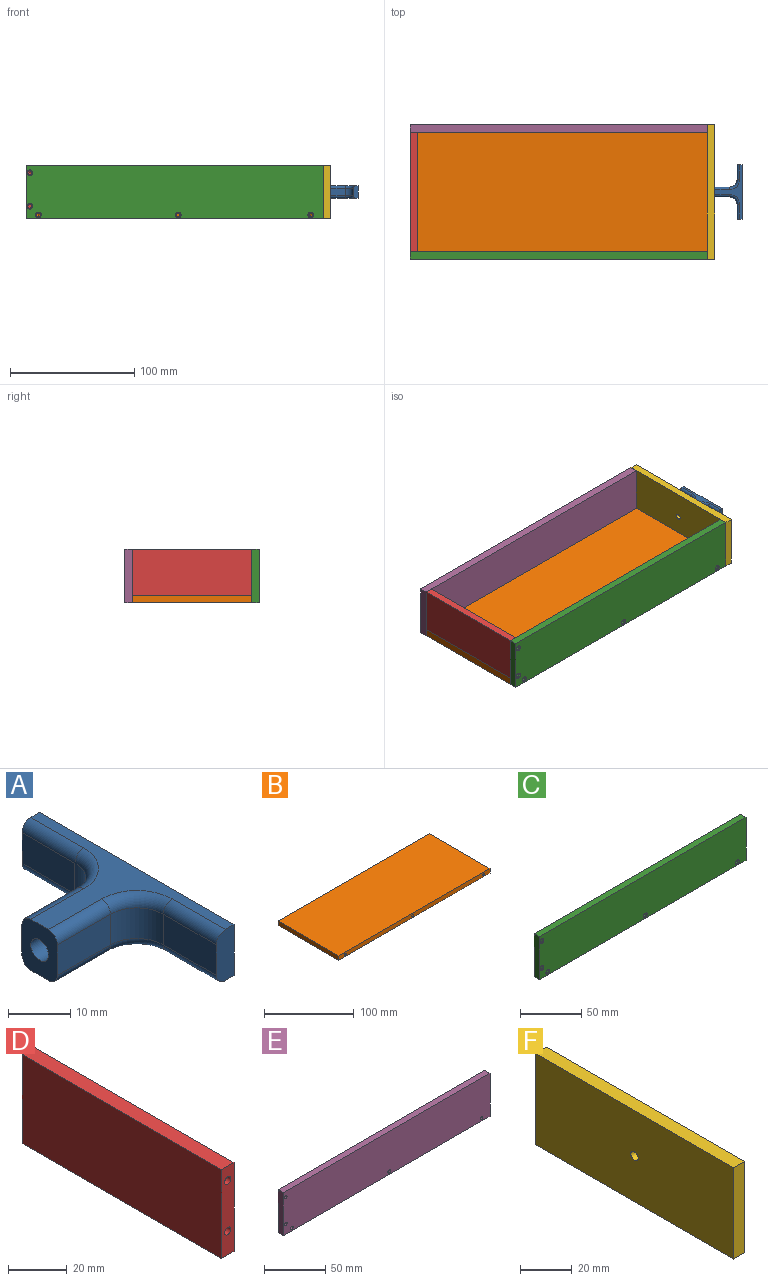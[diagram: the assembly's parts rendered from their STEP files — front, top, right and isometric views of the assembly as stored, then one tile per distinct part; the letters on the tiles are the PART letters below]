
ASSEMBLY  parts=6 mates=11
PART A: 26 faces, bbox 22.2x44x10 mm
  f0: plane 44x10mm, normal (1,0,0), area 440mm2, adj f1,f9,f10,f11
  f1: plane 10x4mm, normal (0,1,0), area 38.3mm2, adj f0,f2,f10,f11,f12,f20
  f2: plane 12x6mm, normal (-1,0,0), area 72mm2, adj f1,f3,f12,f20
  f3: cylinder r=6mm len=6mm, axis (0,0,-1), area 56.5mm2, adj f2,f4,f13,f19
  f4: plane 12x6mm, normal (0,1,0), area 72mm2, adj f3,f5,f14,f18
  f5: plane 10x8mm, normal (-1,0,0), area 64mm2, adj f4,f6,f10,f11,f14,f15,f18,f21
  f6: plane 12x6mm, normal (0,-1,0), area 72mm2, adj f5,f7,f15,f21
  f7: cylinder r=6mm len=6mm, axis (0,0,-1), area 56.5mm2, adj f6,f8,f16,f22
  f8: plane 12x6mm, normal (-1,0,0), area 72mm2, adj f7,f9,f17,f23
  f9: plane 10x4mm, normal (0,-1,0), area 38.3mm2, adj f0,f8,f10,f11,f17,f23
  f10: plane 44x22mm, normal (0,0,1), area 195.5mm2, adj f0,f1,f5,f9,f12,f13,f14,f21
  f11: plane 44x22mm, normal (0,0,-1), area 195.5mm2, adj f0,f1,f5,f9,f15,f16,f17,f18
  f12: cylinder r=2mm len=12mm, axis (0,1,0), area 37.7mm2, adj f1,f2,f10,f13
  f13: torus R=8mm, axis (0,0,1), area 33.2mm2, adj f3,f10,f12,f14
  f14: cylinder r=2mm len=12mm, axis (1,0,0), area 37.7mm2, adj f4,f5,f10,f13
  f15: cylinder r=2mm len=12mm, axis (1,0,0), area 37.7mm2, adj f5,f6,f11,f16
  f16: torus R=8mm, axis (0,0,1), area 33.2mm2, adj f7,f11,f15,f17
  f17: cylinder r=2mm len=12mm, axis (0,-1,0), area 37.7mm2, adj f8,f9,f11,f16
  f18: cylinder r=2mm len=12mm, axis (-1,0,0), area 37.7mm2, adj f4,f5,f11,f19
  f19: torus R=8mm, axis (0,0,1), area 33.2mm2, adj f3,f11,f18,f20
  f20: cylinder r=2mm len=12mm, axis (0,-1,0), area 37.7mm2, adj f1,f2,f11,f19
  f21: cylinder r=2mm len=12mm, axis (-1,0,0), area 37.7mm2, adj f5,f6,f10,f22
  f22: torus R=8mm, axis (0,0,1), area 33.2mm2, adj f7,f10,f21,f23
  f23: cylinder r=2mm len=12mm, axis (0,1,0), area 37.7mm2, adj f8,f9,f10,f22
  f24: cylinder r=2mm len=15mm, axis (-1,0,0), area 188.5mm2, adj f5,f25
  f25: cone r=0mm half-angle=59deg, axis (-1,0,0), area 14.7mm2, adj f24
PART B: 18 faces, bbox 239x96x6 mm
  f0: plane 239x6mm, normal (0,1,0), area 1412.8mm2, adj f1,f3,f4,f5,f12,f14,f16
  f1: plane 96x6mm, normal (-1,0,0), area 576mm2, adj f0,f2,f4,f5
  f2: plane 239x6mm, normal (0,-1,0), area 1412.8mm2, adj f1,f3,f4,f5,f6,f8,f10
  f3: plane 96x6mm, normal (1,0,0), area 576mm2, adj f0,f2,f4,f5
  f4: plane 239x96mm, normal (0,0,1), area 22944mm2, adj f0,f1,f2,f3
  f5: plane 239x96mm, normal (0,0,-1), area 22944mm2, adj f0,f1,f2,f3
  f6: cylinder r=1.5mm len=20mm, axis (0,-1,0), area 188.5mm2, adj f2,f7
  f7: cone r=0mm half-angle=59deg, axis (0,-1,0), area 8.2mm2, adj f6
  f8: cylinder r=1.5mm len=20mm, axis (0,-1,0), area 188.5mm2, adj f2,f9
  f9: cone r=0mm half-angle=59deg, axis (0,-1,0), area 8.2mm2, adj f8
  f10: cylinder r=1.5mm len=20mm, axis (0,-1,0), area 188.5mm2, adj f2,f11
  f11: cone r=0mm half-angle=59deg, axis (0,-1,0), area 8.2mm2, adj f10
  f12: cylinder r=1.5mm len=20mm, axis (0,1,0), area 188.5mm2, adj f0,f13
  f13: cone r=0mm half-angle=59deg, axis (0,1,0), area 8.2mm2, adj f12
  f14: cylinder r=1.5mm len=20mm, axis (0,1,0), area 188.5mm2, adj f0,f15
  f15: cone r=0mm half-angle=59deg, axis (0,1,0), area 8.2mm2, adj f14
  f16: cylinder r=1.5mm len=20mm, axis (0,1,0), area 188.5mm2, adj f0,f17
  f17: cone r=0mm half-angle=59deg, axis (0,1,0), area 8.2mm2, adj f16
PART C: 20 faces, bbox 239x6x43 mm
  f0: plane 239x43mm, normal (0,1,0), area 10241.7mm2, adj f1,f3,f4,f5,f10,f12,f14,f16
  f1: plane 43x6mm, normal (-1,0,0), area 258mm2, adj f0,f2,f4,f5
  f2: plane 239x43mm, normal (0,-1,0), area 10197.5mm2, adj f1,f3,f4,f5,f11,f13,f15,f17
  f3: plane 43x6mm, normal (1,0,0), area 243.9mm2, adj f0,f2,f4,f5,f6,f8
  f4: plane 239x6mm, normal (0,0,1), area 1434mm2, adj f0,f1,f2,f3
  f5: plane 239x6mm, normal (0,0,-1), area 1434mm2, adj f0,f1,f2,f3
  f6: cylinder r=1.5mm len=12mm, axis (1,0,0), area 113.1mm2, adj f3,f7
  f7: cone r=0mm half-angle=59deg, axis (1,0,0), area 8.2mm2, adj f6
  f8: cylinder r=1.5mm len=12mm, axis (1,0,0), area 113.1mm2, adj f3,f9
  f9: cone r=0mm half-angle=59deg, axis (1,0,0), area 8.2mm2, adj f8
  f10: cylinder r=1.5mm len=5.25mm, axis (0,-1,0), area 49.5mm2, adj f0,f11
  f11: cone r=1.5mm half-angle=45deg, axis (0,-1,0), area 12.5mm2, adj f2,f10
  f12: cylinder r=1.5mm len=5.25mm, axis (0,-1,0), area 49.5mm2, adj f0,f13
  f13: cone r=1.5mm half-angle=45deg, axis (0,-1,0), area 12.5mm2, adj f2,f12
  f14: cylinder r=1.5mm len=5.25mm, axis (0,-1,0), area 49.5mm2, adj f0,f15
  f15: cone r=1.5mm half-angle=45deg, axis (0,-1,0), area 12.5mm2, adj f2,f14
  f16: cylinder r=1.5mm len=5.25mm, axis (0,-1,0), area 49.5mm2, adj f0,f17
  f17: cone r=1.5mm half-angle=45deg, axis (0,-1,0), area 12.5mm2, adj f2,f16
  f18: cylinder r=1.5mm len=5.25mm, axis (0,-1,0), area 49.5mm2, adj f0,f19
  f19: cone r=1.5mm half-angle=45deg, axis (0,-1,0), area 12.5mm2, adj f2,f18
PART D: 14 faces, bbox 6x96x37 mm
  f0: plane 37x6mm, normal (0,1,0), area 207.9mm2, adj f1,f3,f4,f5,f10,f12
  f1: plane 96x37mm, normal (-1,0,0), area 3552mm2, adj f0,f2,f4,f5
  f2: plane 37x6mm, normal (0,-1,0), area 207.9mm2, adj f1,f3,f4,f5,f6,f8
  f3: plane 96x37mm, normal (1,0,0), area 3552mm2, adj f0,f2,f4,f5
  f4: plane 96x6mm, normal (0,0,1), area 576mm2, adj f0,f1,f2,f3
  f5: plane 96x6mm, normal (0,0,-1), area 576mm2, adj f0,f1,f2,f3
  f6: cylinder r=1.5mm len=15mm, axis (0,-1,0), area 141.4mm2, adj f2,f7
  f7: cone r=0mm half-angle=59deg, axis (0,-1,0), area 8.2mm2, adj f6
  f8: cylinder r=1.5mm len=15mm, axis (0,-1,0), area 141.4mm2, adj f2,f9
  f9: cone r=0mm half-angle=59deg, axis (0,-1,0), area 8.2mm2, adj f8
  f10: cylinder r=1.5mm len=15mm, axis (0,1,0), area 141.4mm2, adj f0,f11
  f11: cone r=0mm half-angle=59deg, axis (0,1,0), area 8.2mm2, adj f10
  f12: cylinder r=1.5mm len=15mm, axis (0,1,0), area 141.4mm2, adj f0,f13
  f13: cone r=0mm half-angle=59deg, axis (0,1,0), area 8.2mm2, adj f12
PART E: 20 faces, bbox 239x6x43 mm
  f0: plane 239x43mm, normal (0,1,0), area 10197.5mm2, adj f1,f3,f4,f5,f7,f9,f11,f17
  f1: plane 43x6mm, normal (-1,0,0), area 258mm2, adj f0,f2,f4,f5
  f2: plane 239x43mm, normal (0,-1,0), area 10241.7mm2, adj f1,f3,f4,f5,f6,f8,f10,f16
  f3: plane 43x6mm, normal (1,0,0), area 243.9mm2, adj f0,f2,f4,f5,f12,f14
  f4: plane 239x6mm, normal (0,0,1), area 1434mm2, adj f0,f1,f2,f3
  f5: plane 239x6mm, normal (0,0,-1), area 1434mm2, adj f0,f1,f2,f3
  f6: cylinder r=1.5mm len=5.25mm, axis (0,1,0), area 49.5mm2, adj f2,f7
  f7: cone r=1.5mm half-angle=45deg, axis (0,1,0), area 12.5mm2, adj f0,f6
  f8: cylinder r=1.5mm len=5.25mm, axis (0,1,0), area 49.5mm2, adj f2,f9
  f9: cone r=1.5mm half-angle=45deg, axis (0,1,0), area 12.5mm2, adj f0,f8
  f10: cylinder r=1.5mm len=5.25mm, axis (0,1,0), area 49.5mm2, adj f2,f11
  f11: cone r=1.5mm half-angle=45deg, axis (0,1,0), area 12.5mm2, adj f0,f10
  f12: cylinder r=1.5mm len=12mm, axis (1,0,0), area 113.1mm2, adj f3,f13
  f13: cone r=0mm half-angle=59deg, axis (1,0,0), area 8.2mm2, adj f12
  f14: cylinder r=1.5mm len=12mm, axis (1,0,0), area 113.1mm2, adj f3,f15
  f15: cone r=0mm half-angle=59deg, axis (1,0,0), area 8.2mm2, adj f14
  f16: cylinder r=1.5mm len=5.25mm, axis (0,1,0), area 49.5mm2, adj f2,f17
  f17: cone r=1.5mm half-angle=45deg, axis (0,1,0), area 12.5mm2, adj f0,f16
  f18: cylinder r=1.5mm len=5.25mm, axis (0,1,0), area 49.5mm2, adj f2,f19
  f19: cone r=1.5mm half-angle=45deg, axis (0,1,0), area 12.5mm2, adj f0,f18
PART F: 7 faces, bbox 6x108x43 mm
  f0: plane 108x6mm, normal (0,0,1), area 648mm2, adj f1,f3,f4,f5
  f1: plane 43x6mm, normal (0,-1,0), area 258mm2, adj f0,f2,f4,f5
  f2: plane 108x6mm, normal (0,0,-1), area 648mm2, adj f1,f3,f4,f5
  f3: plane 43x6mm, normal (0,1,0), area 258mm2, adj f0,f2,f4,f5
  f4: plane 108x43mm, normal (1,0,0), area 4631.4mm2, adj f0,f1,f2,f3,f6
  f5: plane 108x43mm, normal (-1,0,0), area 4631.4mm2, adj f0,f1,f2,f3,f6
  f6: cylinder r=2mm len=6mm, axis (1,0,0), area 75.4mm2, adj f4,f5
PLACE A t=(199.26,36.65,23.65)mm
PLACE B t=(-67.74,-11.35,7.15)mm fixed
PLACE C t=(-67.74,-17.35,7.15)mm
PLACE D t=(-67.74,-11.35,13.15)mm
PLACE E t=(-67.74,84.65,7.15)mm
PLACE F t=(171.26,-17.35,7.15)mm
MATE revolute D.f6 <-> C.f10  axis (0,-1,0) through (-64.74,-11.35,44.15)mm
MATE planar D.f1 <-> E.f1  axis (-1,0,0) through (-67.74,36.65,31.65)mm
MATE planar F.f6 <-> E.f3  axis (-1,0,0) through (171.26,36.65,28.65)mm
MATE planar F.f1 <-> C.f2  axis (0,-1,0) through (174.26,-17.35,28.65)mm
MATE parallel A.f10 <-> F.f0  axis (0,0,1) through (199.26,36.65,33.65)mm
MATE revolute C.f18 <-> B.f6  axis (0,1,0) through (-57.74,-11.35,10.15)mm
MATE planar F.f2 <-> B.f5  axis (0,0,-1) through (174.26,36.65,7.15)mm
MATE revolute E.f10 <-> B.f6  axis (0,-1,0) through (-57.74,84.65,10.15)mm
MATE revolute E.f6 <-> B.f10  axis (0,-1,0) through (161.26,84.65,10.15)mm
MATE revolute F.f6 <-> A.f25  axis (1,0,0) through (177.26,36.65,28.65)mm
MATE revolute B.f10 <-> C.f16  axis (0,-1,0) through (161.26,-11.35,10.15)mm
